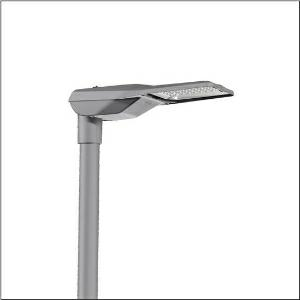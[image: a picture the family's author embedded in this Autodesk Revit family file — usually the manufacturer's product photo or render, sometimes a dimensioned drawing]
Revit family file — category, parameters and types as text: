
# Revit family: streetlight_sl_21_iq_mini___p0_5a_5xe2v31v08jb_ab6f
name_source: partatom
category: Lighting Fixtures
units: mm (PartAtom-declared; Revit-internal decimal feet)

## family parameters
Cut with Voids When Loaded = No
Host = Face
Light Source = No
Part Type = Normal
Room Calculation Point = No
Round Connector Dimension = Use Diameter
Shared = No

## types (1)
- --- (1 x LED, 11020 lm, 72.5 W, 3000K)
    Apparent Load = 73 VA
    CIE Flux Codes = 37 73 96 100 100
    Color Rendering = 70
    Color Temperature = 3000K
    Default Elevation = 1800 mm
    Description = Streetlight SL 21 iQ mini, mast luminaire, primary light control with lens, of PMMA, primary optical cover: cover, of toughened safety glass, transparent, light distribution: P0.5a, light emission: direct distribution, primary light characteristic: asymmetric, installation type: post-top, side-entry, LED, High Power LED, rated luminous flux: 11.020lm, luminous efficacy: 152lm/W, light colour: 730, colour temperature: 3000K, control gear: iQ-Street Remote, D4i with power reduction, control: pre-setting: logarithmic dimming characteristic, Street-Remote, Auto-Match, Temp-Guard, Lumen-Switch, Night-Set, Smart-Wire, Light-Fading, Desk-Remote (wireless, voltage-free reading and setting of iQ features in the workshop via application-optimized NFC function/RFID function), optimised constant luminous flux control (CLO 2.0), mains connection: 220..240V, AC, 50/60Hz, start of lifetime: 73W, end of service life: 76W, reduction: 33W, luminaire housing, of diecast aluminium, powder-coated, Siteco® metallic grey (DB 702S), corrosivity category C5 mid according to DIN EN ISO 12944, please order mast flange separately, inclination adjustable: 0°, 5°, 10°, 15°, sealing non-destructively replaceable, multi-level sealing system, length: 628mm, width: 235mm, height: 110mm, mast flange for spigot size: 42mm (side-entry): 5XC10008XM4, 60/48mm (side-entry/post-top): 5XC10108XM2, 76/60mm (side-entry/post-top): 5XC10108XM1, mounting height: 4..8m, Smart Interface above, protection rating (complete): IP66, insulation class (complete): insulation class II (safety insulation), certification: CE, ENEC, ENEC+, VDE, impact resistance: IK10, permissible operating ambient temperature for outdoor applications: -40..+50°C, standard-compliant lighting for roads and squares, packaging unit: 1 piece

Light Distribution: P0.5a
    Height = 110 mm
    Lamp = 1 x LED
    Lamp Light Flux = 11020 lm
    Lamp Power = 72.5 W
    Lamp count = 1
    Length = 625 mm
    Luminous efficacy = 152 lm/W
    Manufacturer = Siteco
    ModVariant = No
    Model = 5XE2V31V08JB
    Number of Poles = 1
    OnlyDefault = Yes
    Power Factor = 1
    Product Name = Streetlight SL 21 iQ mini | P0.5a
    Product group = mast luminaire | pylon top
    ProductGroupID = 6100
    Protection Class = Protection class II
    Protection Degree = IP 66
    RLX_Detail_Level = 1
    RLX_Emergency_Light_Flux = 0 lm
    RLX_Emergency_Type = 0
    RLX_Emergency_Type_DB = No
    RlxData = <blob elided: 92113 chars, md5=0579fa53>
    Socket = socket
    Standby Power = 0 W
    System Light Flux = 11020 lm
    System Power = 73 W
    Type Comments = factory setting: luminous flux: 100 % | dim-lin: 254 | 755 mA
    Type Image = l_1003515.jpg
    URL = http://relux.com
    VarID = @adj_090949
    Voltage = 0 V
    Weight = 0.00 kg
    Width = 234 mm

## geometry (parser evidence)
native form markers: Blend x4, Sweep x10
no freeform markers — native parametric forms only
